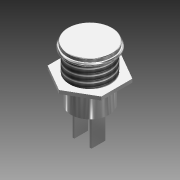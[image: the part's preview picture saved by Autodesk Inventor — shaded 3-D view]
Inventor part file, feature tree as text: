
AUTODESK INVENTOR PART (.ipt)
format: ipt  version: 2013 SP1 (Build 170176100, 176)  size: 220,672 bytes
history: native  units: mm
features: sketch x7, extrude x6, other x6, fillet x2, thread x1, revolve x1
ambient origin geometry x8: Origin, YZ Plane, XZ Plane, XY Plane, X Axis, Y Axis, Z Axis, Center Point
bodies: Volumenkörper1 (feature_tree), Volumenkörper2 (feature_tree), Volumenkörper3 (feature_tree), Volumenkörper4 (feature_tree), Volumenkörper6 (feature_tree), Volumenkörper7 (feature_tree)
feature tree (23):
  extrude  "Extrusion1"  Depth=6.0mm TaperAngle=0.0deg
  extrude  "Extrusion2"  Depth=8.0mm TaperAngle=0.0deg
  thread  "Gewinde1"  [1 undecoded]
  extrude  "Extrusion3"  Depth=1.0mm TaperAngle=0.0deg
  other  "Körper verschieben1"
  fillet  "Rundung1"  Radius=13.0mm
  extrude  "Extrusion4"  Depth=9.0mm TaperAngle=0.0deg
  other  "Körper verschieben2"
  fillet  "Rundung2"  Radius=1.0mm
  revolve  "Umdrehung1"
  other  "Körper verschieben3"
  extrude  "Extrusion5"  TaperAngle=90.0deg  [1 undecoded]
  other  "Körper verschieben4"
  extrude  "Extrusion6"  Depth=12.0mm
  other  "Körper verschieben5"
  sketch  "Skizze1"  dims[d0=11.0mm d1=6.0mm d2=0.0mm]
  sketch  "Skizze2"  dims[d5=12.0mm d6=8.0mm d7=0.0mm d8=10.0mm d9=0.0mm]
  sketch  "Skizze3"  dims[d10=11.5mm d11=1.0mm d12=0.0mm]
  sketch  "Skizze4"  dims[d13=0.0mm d14=0.0mm d15=8.0mm d17=0.5mm d19=13.0mm]
  sketch  "Skizze5"  dims[d20=1.0mm d21=0.0mm d22=0.0mm d23=0.0mm d24=9.0mm d25=0.25mm d26=1.0mm]
  other  "Volumenkörper Unterlegscheibe"
  sketch  "Skizze6"  dims[d27=6.5mm d28=90.0deg]
  sketch  "Skizze7"  dims[d29=0.0mm d30=0.0mm d31=8.5mm d32=12.0mm d33=1.0mm d34=0.0mm d35=0.0mm d36=0.0mm d37=1.0mm d38=0.5mm d39=4.0mm d40=0.5mm d41=4.0mm d42=9.0mm d43=0.0mm d44=0.0mm d45=0.0mm d46=-6.0mm]
note: 2 required parameter values undecoded (feature->parameter linkage not recoverable at this tier; creation-order binding heuristic only, values carry confidence <= 0.55)
